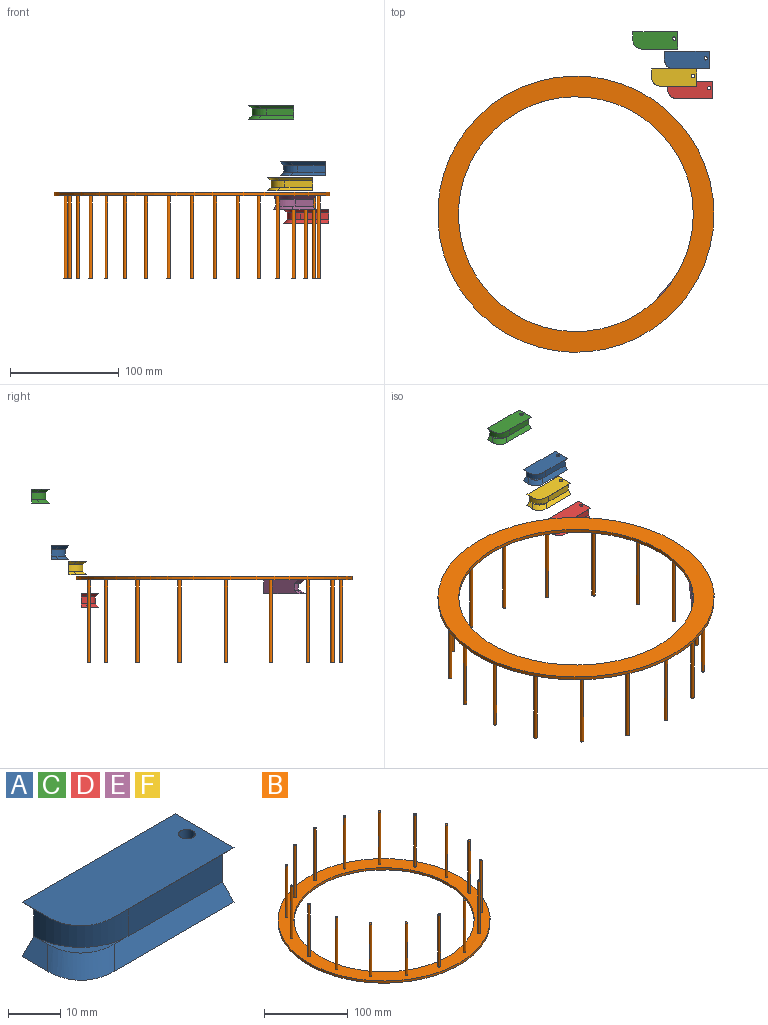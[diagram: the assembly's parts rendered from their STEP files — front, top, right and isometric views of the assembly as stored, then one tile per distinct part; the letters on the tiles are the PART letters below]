
ASSEMBLY  parts=6 mates=1
PART A: 15 faces, bbox 42.7x17.3x15.5 mm
  f0: plane 25.4x6.35mm, normal (0,-1,0), area 161.3mm2, adj f1,f3,f9,f12
  f1: plane 15.88x12.7mm, normal (1,0,0), area 171.4mm2, adj f0,f2,f5,f7,f9,f12
  f2: plane 41.28x12.7mm, normal (0,1,0), area 494mm2, adj f1,f3,f5,f7,f10,f11
  f3: cylinder r=12.7mm len=12.7mm, axis (0,0,-1), area 126.7mm2, adj f0,f2,f4,f6
  f4: plane 12.7x12.7mm, normal (0,0,-1), area 19.6mm2, adj f3,f11,f12,f13
  f5: plane 41.28x15.88mm, normal (0,0,1), area 632.3mm2, adj f1,f2,f8,f11,f12,f13
  f6: plane 12.7x12.7mm, normal (0,0,1), area 19.6mm2, adj f3,f9,f10,f14
  f7: plane 41.28x15.88mm, normal (0,0,-1), area 632.3mm2, adj f1,f2,f8,f9,f10,f14
  f8: cylinder r=1.59mm len=12.7mm, axis (0,0,1), area 126.7mm2, adj f5,f7
  f9: plane 32.29x3.18mm, normal (0,-0.71,0.71), area 137.9mm2, adj f0,f1,f6,f7,f14
  f10: plane 6.89x3.18mm, normal (-0.71,0,0.71), area 23.8mm2, adj f2,f6,f7,f14
  f11: plane 6.89x3.18mm, normal (-0.71,0,-0.71), area 23.8mm2, adj f2,f4,f5,f13
  f12: plane 32.29x3.18mm, normal (0,-0.71,-0.71), area 137.9mm2, adj f0,f1,f4,f5,f13
  f13: cylinder r=12.7mm len=13.55mm, axis (-0.58,-0.58,0.58), area 73.1mm2, adj f4,f5,f11,f12
  f14: cylinder r=12.7mm len=13.55mm, axis (-0.58,-0.58,-0.58), area 73.1mm2, adj f6,f7,f9,f10
PART B: 38 faces, bbox 254x254x79.4 mm
  f0: cylinder r=107.95mm len=215.9mm, axis (0,0,-1), area 2153.5mm2, adj f2,f3
  f1: cylinder r=127mm len=254mm, axis (0,0,-1), area 2533.5mm2, adj f2,f3
  f2: plane 254x254mm, normal (0,0,1), area 13926.5mm2, adj f0,f1,f4,f6,f8,f10,f12,f14
  f3: plane 254x254mm, normal (0,0,-1), area 14061.1mm2, adj f0,f1
  f4: cylinder r=1.59mm len=76.2mm, axis (0,0,-1), area 760.1mm2, adj f2,f5
  f5: plane 3.18x3.18mm, normal (0,0,1), area 7.9mm2, adj f4
  f6: cylinder r=1.59mm len=76.2mm, axis (0,0,-1), area 760.1mm2, adj f2,f7
  f7: plane 3.18x3.18mm, normal (0,0,1), area 7.9mm2, adj f6
  f8: cylinder r=1.59mm len=76.2mm, axis (0,0,-1), area 760.1mm2, adj f2,f9
  f9: plane 3.18x3.18mm, normal (0,0,1), area 7.9mm2, adj f8
  f10: cylinder r=1.59mm len=76.2mm, axis (0,0,-1), area 760.1mm2, adj f2,f11
  f11: plane 3.18x3.18mm, normal (0,0,1), area 7.9mm2, adj f10
  f12: cylinder r=1.59mm len=76.2mm, axis (0,0,-1), area 760.1mm2, adj f2,f13
  f13: plane 3.18x3.18mm, normal (0,0,1), area 7.9mm2, adj f12
  f14: cylinder r=1.59mm len=76.2mm, axis (0,0,-1), area 760.1mm2, adj f2,f15
  f15: plane 3.18x3.18mm, normal (0,0,1), area 7.9mm2, adj f14
  f16: cylinder r=1.59mm len=76.2mm, axis (0,0,-1), area 760.1mm2, adj f2,f17
  f17: plane 3.18x3.18mm, normal (0,0,1), area 7.9mm2, adj f16
  f18: cylinder r=1.59mm len=76.2mm, axis (0,0,-1), area 760.1mm2, adj f2,f19
  f19: plane 3.18x3.18mm, normal (0,0,1), area 7.9mm2, adj f18
  f20: cylinder r=1.59mm len=76.2mm, axis (0,0,-1), area 760.1mm2, adj f2,f21
  f21: plane 3.18x3.18mm, normal (0,0,1), area 7.9mm2, adj f20
  f22: cylinder r=1.59mm len=76.2mm, axis (0,0,-1), area 760.1mm2, adj f2,f23
  f23: plane 3.18x3.18mm, normal (0,0,1), area 7.9mm2, adj f22
  f24: cylinder r=1.59mm len=76.2mm, axis (0,0,-1), area 760.1mm2, adj f2,f25
  f25: plane 3.18x3.18mm, normal (0,0,1), area 7.9mm2, adj f24
  f26: cylinder r=1.59mm len=76.2mm, axis (0,0,-1), area 760.1mm2, adj f2,f27
  f27: plane 3.18x3.18mm, normal (0,0,1), area 7.9mm2, adj f26
  f28: cylinder r=1.59mm len=76.2mm, axis (0,0,-1), area 760.1mm2, adj f2,f29
  f29: plane 3.18x3.18mm, normal (0,0,1), area 7.9mm2, adj f28
  f30: cylinder r=1.59mm len=76.2mm, axis (0,0,-1), area 760.1mm2, adj f2,f31
  f31: plane 3.18x3.18mm, normal (0,0,1), area 7.9mm2, adj f30
  f32: cylinder r=1.59mm len=76.2mm, axis (0,0,-1), area 760.1mm2, adj f2,f33
  f33: plane 3.18x3.18mm, normal (0,0,1), area 7.9mm2, adj f32
  f34: cylinder r=1.59mm len=76.2mm, axis (0,0,-1), area 760.1mm2, adj f2,f35
  f35: plane 3.18x3.18mm, normal (0,0,1), area 7.9mm2, adj f34
  f36: cylinder r=1.59mm len=76.2mm, axis (0,0,-1), area 760.1mm2, adj f2,f37
  f37: plane 3.18x3.18mm, normal (0,0,1), area 7.9mm2, adj f36
PART C: same geometry as A
PART D: same geometry as A
PART E: same geometry as A
PART F: same geometry as A
PLACE A t=(73.37,48.01,30.31)mm
PLACE B rot(axis=(-1,0,0),180deg) t=(-49.29,-88.92,11.7)mm fixed
PLACE C t=(44.32,65.97,82.42)mm
PLACE D t=(76.38,20.55,-13.48)mm
PLACE E rot(axis=(0,0,1),49.1deg) t=(62.18,-142.76,-1)mm
PLACE F t=(61.65,31.9,16.3)mm
MATE revolute E.f8 <-> B.f32  axis (0,0,1) through (55.3,-141,8.52)mm
